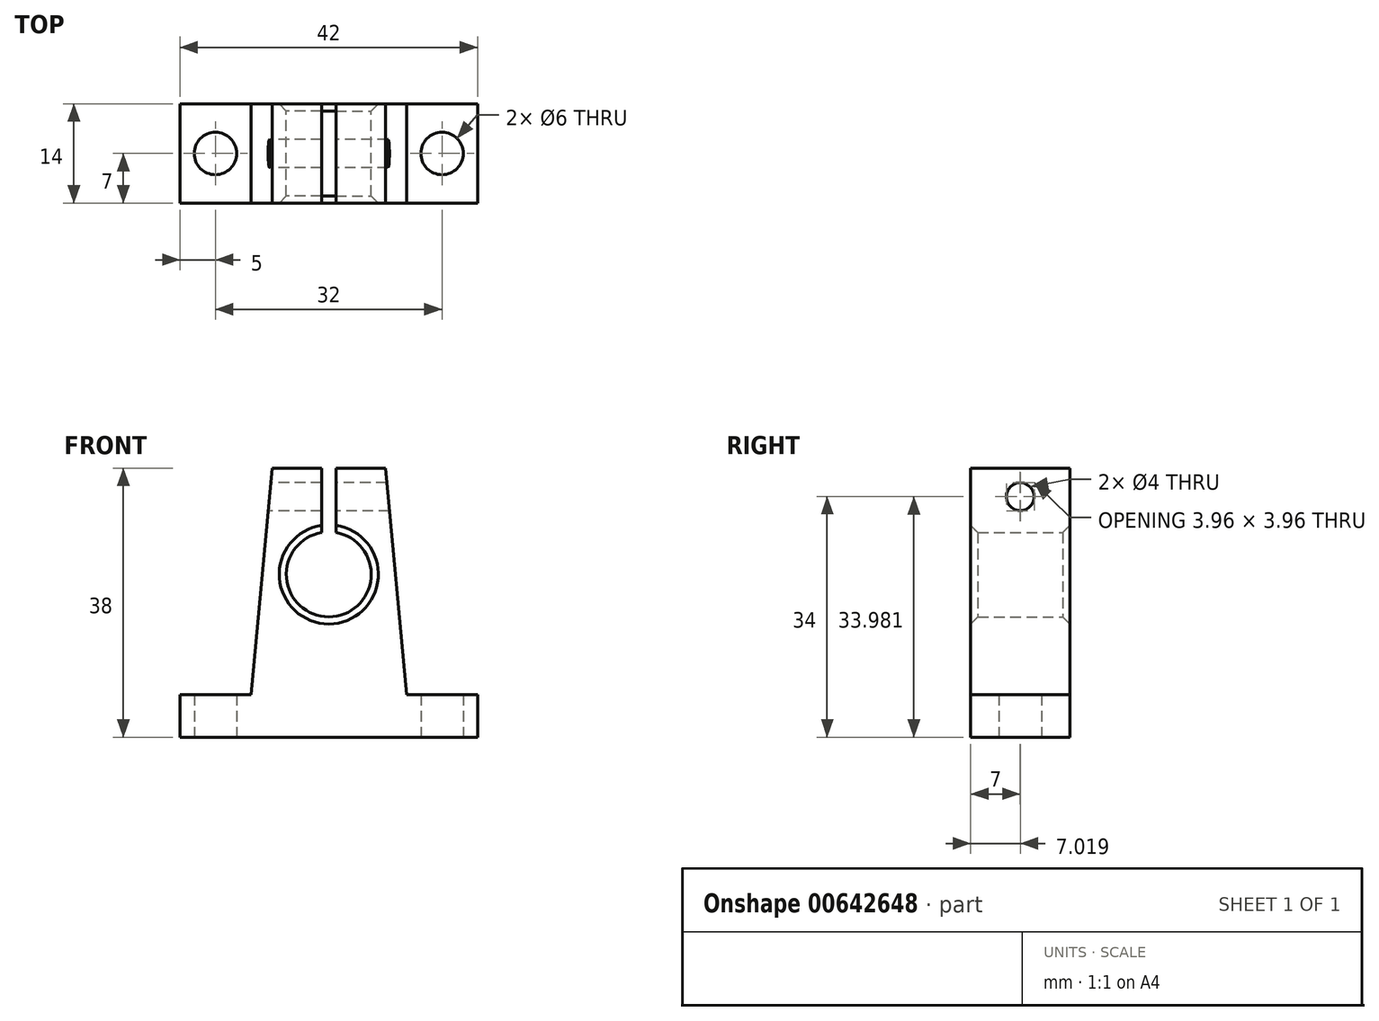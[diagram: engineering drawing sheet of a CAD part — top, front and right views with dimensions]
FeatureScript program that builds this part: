
annotation { "Feature Type Name" : "Feature", "Feature Type Description" : "" }
export const myFeature = defineFeature(function(context is Context, id is Id, definition is map)
    precondition{}
    {
        {
            var Q0;
            Q0=qCreatedBy(makeId("Top.planeOp"),FACE);
            var sketch = newSketch(context, id + "F0", { "sketchPlane" : qUnion([Q0])});
            skLineSegment(sketch, "E0", {"start": v(-21, 0) * mm, "end": v(21, 0) * mm});
            skLineSegment(sketch, "E1", {"start": v(21, 0) * mm, "end": v(21, 6) * mm});
            skLineSegment(sketch, "E2", {"start": v(21, 6) * mm, "end": v(11, 6) * mm});
            skLineSegment(sketch, "E3", {"start": v(11, 6) * mm, "end": v(8, 38) * mm});
            skLineSegment(sketch, "E4", {"start": v(8, 38) * mm, "end": v(-8, 38) * mm});
            skLineSegment(sketch, "E5", {"start": v(-8, 38) * mm, "end": v(-11, 6) * mm});
            skLineSegment(sketch, "E6", {"start": v(-11, 6) * mm, "end": v(-21, 6) * mm});
            skLineSegment(sketch, "E7", {"start": v(-21, 6) * mm, "end": v(-21, 0) * mm});
            skCircle(sketch, "E8", {"center": v(0, 23) * mm, "radius": 6 * mm});
            skLineSegment(sketch, "E9", {"start": v(0, 38) * mm, "end": v(-1, 38) * mm});
            skLineSegment(sketch, "E10.bottom", {"start": v(-1, 38) * mm, "end": v(1, 38) * mm});
            skLineSegment(sketch, "E10.top", {"start": v(-1, 28.92) * mm, "end": v(1, 28.92) * mm});
            skLineSegment(sketch, "E10.left", {"start": v(-1, 38) * mm, "end": v(-1, 28.92) * mm});
            skLineSegment(sketch, "E10.right", {"start": v(1, 38) * mm, "end": v(1, 28.92) * mm});
            skPoint(sketch, "E11.visualSharp", {"position": v(-11, 6) * mm});
            skPoint(sketch, "E12.visualSharp", {"position": v(11, 6) * mm});
            skPoint(sketch, "E13.visualSharp", {"position": v(-8, 38) * mm});
            skPoint(sketch, "E14.visualSharp", {"position": v(8, 38) * mm});
            skPoint(sketch, "E15.visualSharp", {"position": v(-21, 6) * mm});
            skPoint(sketch, "E16.visualSharp", {"position": v(21, 6) * mm});
            skPoint(sketch, "E17", {"position": v(0, 0) * mm});
            skSolve(sketch);
        }
        {
            var Q0;
            Q0=makeQuery(id+"F0.imprint","IMPRINT",FACE,{"disambiguationData":[TD([[makeQuery(id+"F0.imprint","IMPRINT",EDGE,{"derivedFrom":sQuery(id+"F0.wireOp",EDGE,"E0")}),1.0]])]});
            extrude(context, id + "F1", {"entities" : qUnion([Q0]), "depth" : 14 * mm});
        }
        {
            var Q0;
            Q0=makeQuery(id+"F1.opExtrude","SWEPT_FACE",FACE,{"disambiguationData":[OSD([sQuery(id+"F0.wireOp",EDGE,"E0")])]});
            var sketch = newSketch(context, id + "F2", { "sketchPlane" : qUnion([Q0])});
            skPoint(sketch, "E18", {"position": v(0, 7) * mm});
            skCircle(sketch, "E19", {"center": v(-16, 7) * mm, "radius": 3 * mm});
            skCircle(sketch, "E20", {"center": v(16, 7) * mm, "radius": 3 * mm});
            skLineSegment(sketch, "E21", {"start": v(0, 14) * mm, "end": v(0, 0) * mm, "construction": true});
            skLineSegment(sketch, "E22", {"start": v(-16, 7) * mm, "end": v(0, 7) * mm, "construction": true});
            skLineSegment(sketch, "E23", {"start": v(0, 7) * mm, "end": v(16, 7) * mm, "construction": true});
            skSolve(sketch);
        }
        {
            var Q0;
            Q0=qSketchRegion(id+"F2",true);
            extrude(context, id + "F3", {"entities" : qUnion([Q0]), "operationType" : NewBodyOperationType.REMOVE, "endBound" : BoundingType.THROUGH_ALL, "oppositeDirection" : true, "depth" : 25 * mm});
        }
        {
            var Q0;
            Q0=makeQuery(id+"F1.opExtrude","CAP_EDGE",EDGE,{"disambiguationData":[OSD([sQuery(id+"F0.wireOp",EDGE,"E8")])],"isStart":false});
            var Q1;
            Q1=makeQuery(id+"F1.opExtrude","CAP_EDGE",EDGE,{"disambiguationData":[OSD([sQuery(id+"F0.wireOp",EDGE,"E8")])],"isStart":true});
            chamfer(context, id + "F4", {"entities" : qUnion([Q0, Q1]), "width" : 1 * mm, "tangentPropagation" : true});
        }
        {
            var Q0;
            Q0=makeQuery(id+"F1.opExtrude","SWEPT_FACE",FACE,{"disambiguationData":[OSD([sQuery(id+"F0.wireOp",EDGE,"E7")])]});
            var sketch = newSketch(context, id + "F5", { "sketchPlane" : qUnion([Q0])});
            skLineSegment(sketch, "E24.0", {"start": v(-38, 14) * mm, "end": v(-38, 0) * mm});
            skLineSegment(sketch, "E25", {"start": v(-38, 7) * mm, "end": v(-26.17, 7) * mm, "construction": true});
            skCircle(sketch, "E26", {"center": v(-34, 7) * mm, "radius": 2 * mm});
            skSolve(sketch);
        }
        {
            var Q0;
            Q0=qSketchRegion(id+"F5",true);
            extrude(context, id + "F6", {"entities" : qUnion([Q0]), "operationType" : NewBodyOperationType.REMOVE, "endBound" : BoundingType.THROUGH_ALL, "oppositeDirection" : true, "depth" : 25 * mm});
        }
        {
            var Q0;
            Q0=makeQuery(id+"F1.opExtrude","SWEPT_BODY",BODY,{"disambiguationData":[OSD([sQuery(id+"F0.wireOp",EDGE,"E0"),sQuery(id+"F0.wireOp",EDGE,"E1"),sQuery(id+"F0.wireOp",EDGE,"E2"),sQuery(id+"F0.wireOp",EDGE,"E3"),sQuery(id+"F0.wireOp",EDGE,"E4"),sQuery(id+"F0.wireOp",EDGE,"E5"),sQuery(id+"F0.wireOp",EDGE,"E6"),sQuery(id+"F0.wireOp",EDGE,"E7"),sQuery(id+"F0.wireOp",EDGE,"E8"),sQuery(id+"F0.wireOp",EDGE,"E10.left"),sQuery(id+"F0.wireOp",EDGE,"E10.right")])]});
            var Q1;
            Q1=makeQuery(id+"F1.opExtrude","CAP_EDGE",EDGE,{"disambiguationData":[OSD([sQuery(id+"F0.wireOp",EDGE,"E0")])],"isStart":true});
            var Q2;
            Q2=makeQuery(id+"F1.opExtrude","CAP_EDGE",EDGE,{"disambiguationData":[OSD([sQuery(id+"F0.wireOp",EDGE,"E0")])],"isStart":true});
            transform(context, id + "F7", {"entities" : qUnion([Q0]), "transformType" : TransformType.ROTATION, "transformAxis" : qUnion([Q2]), "angle" : 90 * degree, "makeCopy" : false});
        }
    });
